# Revit family: 1RLV-K_Straight_DN15-DN20_RFA
name_source: partatom
category: Pipe Accessories
units: mm (PartAtom-declared; Revit-internal decimal feet)

## family parameters
Always vertical = Yes
Cut with Voids When Loaded = No
OmniClass Number = 23.65.55.14.17
OmniClass Title = Adjusting/Controlling Valves for Liquid Services
Part Type = Valve - Breaks Into
Round Connector Dimension = Use Diameter
Shared = No
Work Plane-Based = No

## types (2) — shared parameters
CC_2 = 25 mm  [stored 0.082021 ft]
CGAP = 50 mm  [stored 0.164042 ft]
CenSd_R5_6 = 14.7 mm
D = 20 mm  [stored 0.0656168 ft]
DN15_LOD 200 = No
Description = H-piece
H6 = 5 mm  [stored 0.0164042 ft]
HB0 = 22 mm  [stored 0.0721785 ft]
HB1 = 8 mm  [stored 0.0262467 ft]
HH = 42 mm  [stored 0.137795 ft]
HH1 = 2 mm  [stored 0.00656168 ft]
HT1 = 28 mm  [stored 0.0918635 ft]
HT2 = 17 mm  [stored 0.0557743 ft]
HT3 = 2.5 mm  [stored 0.0082021 ft]
HT4 = 6 mm  [stored 0.019685 ft]
HT5 = 11 mm  [stored 0.0360892 ft]
IfcExportAs = IfcValveType
IfcExportType = RLV-K
Kvs = 1.4 m³/h
LOD 200 = No
LOD 350 = Yes
L_EQ = 25 mm  [stored 0.082021 ft]
Manufacturer = Danfoss
Max Medium Temperature = 120 ˚C
Max Operating Pressure = 10 bar
NL2 = 17 mm  [stored 0.0557743 ft]
NW1 = 8 mm  [stored 0.0262467 ft]
R11 = 11 mm  [stored 0.0360892 ft]
R2 = 11.5 mm
R4 = 12.8 mm  [stored 0.0419948 ft]
R5 = 17 mm  [stored 0.0557743 ft]
R6 = 11 mm  [stored 0.0360892 ft]
R7 = 10.5 mm  [stored 0.0344488 ft]
RV1 = 11.6 mm
R_1 = 10 mm  [stored 0.0328084 ft]
R_2 = 17 mm  [stored 0.0557743 ft]
TD = 34 mm
URL = https://store.danfoss.com
Valve Body Material = Danfoss Nickel Plated Brass
W1 = 38.5 mm  [stored 0.126312 ft]

## per-type parameters (varying)
| type | DN15_LOD 350 | DR | H | Model | Model Type | RN | RV3 | Weight |
| RLV-K_Straight_DN15-20_003L0280 | Yes | 15 mm | 80.5 mm | 003L0280 | RLV-K_Straight_DN15-20 | 13 mm  [stored 0.0426509 ft] | 12.8 mm  [stored 0.0419948 ft] | 0.58 kg |
| RLV-K_Straight_DN20-20_003L0281 | No | 20 mm | 69.5 mm | 003L0281 | RLV-K_Straight_DN20-20 | 13.3 mm  [stored 0.0436352 ft] | 9 mm  [stored 0.0295276 ft] | 0.50 kg |

note: [stored X ft] marks values corroborated as IEEE doubles in the binary element streams (Revit-internal decimal feet)

## geometry (parser evidence)
native form markers: Sweep x4
no freeform markers — native parametric forms only
